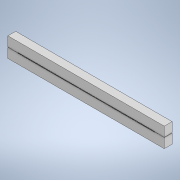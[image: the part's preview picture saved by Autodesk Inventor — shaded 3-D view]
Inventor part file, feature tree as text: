
AUTODESK INVENTOR PART (.ipt)
format: ipt  version: 2021 (Build 250183000, 183)  size: 1,000,960 bytes
history: native  units: in
note: dims shown in document units (in); Inventor stores cm internally (conversion verified against a paired STEP export)
features: extrude x2, sketch x2, projected_geometry x2, pattern_linear x1
ambient origin geometry x8: Origin, YZ Plane, XZ Plane, XY Plane, X Axis, Y Axis, Z Axis, Center Point
bodies: Solid1 (feature_tree)
feature tree (7):
  extrude  "Extrusion1"  Depth=0.4921in
  extrude  "Extrusion3"  Depth=0.1969in TaperAngle=0.0deg
  pattern_linear  "Rectangular Pattern1"  Spacing1=0.0098in  [1 undecoded]
  sketch  "Sketch1"  dims[d0=3.937in d1=0.4921in]
  sketch  "Sketch3"  dims[d2=0.0118in d3=0.1969in d4=0.0in d9=0.0098in d11=0.0049in d12=0.0in d13=0.0in d14=68.8976in d16=0.0197in d19=0.0197in d20=0.0344in d21=0.0197in d22=0.0344in]
  projected_geometry  "Projected Loop3"
  projected_geometry  "Projected Loop4"
note: 1 required parameter value undecoded (feature->parameter linkage not recoverable at this tier; creation-order binding heuristic only, values carry confidence <= 0.55)
